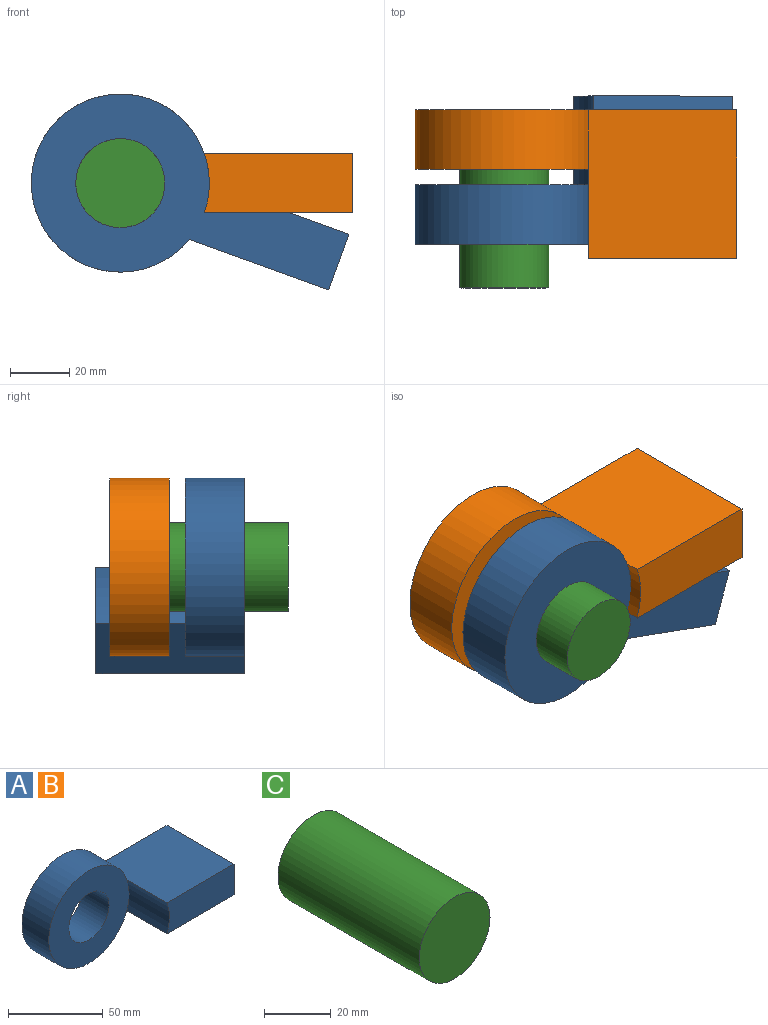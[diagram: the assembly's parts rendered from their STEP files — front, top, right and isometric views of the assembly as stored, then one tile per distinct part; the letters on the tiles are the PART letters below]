
ASSEMBLY  parts=3 mates=2
PART A: 9 faces, bbox 108.3x50x60 mm
  f0: plane 60x60mm, normal (0,-1,0), area 2120.6mm2, adj f2,f5,f7
  f1: plane 50x50mm, normal (0,0,1), area 2500mm2, adj f2,f4,f6,f7,f8
  f2: cylinder r=30mm len=60mm, axis (0,1,0), area 3362.1mm2, adj f0,f1,f3,f6
  f3: plane 50x50mm, normal (0,0,-1), area 2500mm2, adj f2,f4,f6,f7,f8
  f4: plane 50x20mm, normal (1,0,0), area 1000mm2, adj f1,f3,f6,f8
  f5: cylinder r=15mm len=30mm, axis (0,1,0), area 1885mm2, adj f0,f6
  f6: plane 108.28x60mm, normal (0,1,0), area 3097.6mm2, adj f1,f2,f3,f4,f5
  f7: cylinder r=30mm len=30mm, axis (0,1,0), area 611.7mm2, adj f0,f1,f3,f8
  f8: plane 50x20mm, normal (0,-1,0), area 977mm2, adj f1,f3,f4,f7
PART B: same geometry as A
PART C: 3 faces, bbox 30x60x30 mm
  f0: cylinder r=15mm len=60mm, axis (0,1,0), area 5654.9mm2, adj f1,f2
  f1: plane 30x30mm, normal (0,-1,0), area 706.9mm2, adj f0
  f2: plane 30x30mm, normal (0,1,0), area 706.9mm2, adj f0
PLACE A rot(axis=(0.99,0,-0.17),180deg) t=(-1.68,-45.29,-9.61)mm
PLACE B at identity fixed
PLACE C t=(-28.28,0,0)mm
MATE cylindrical B.f2 <-> A.f2  axis (0,-1,0) through (-28.28,-20,0)mm
MATE fastened C.f0 <-> B.f2  axis (0,1,0) through (-28.28,0,0)mm
